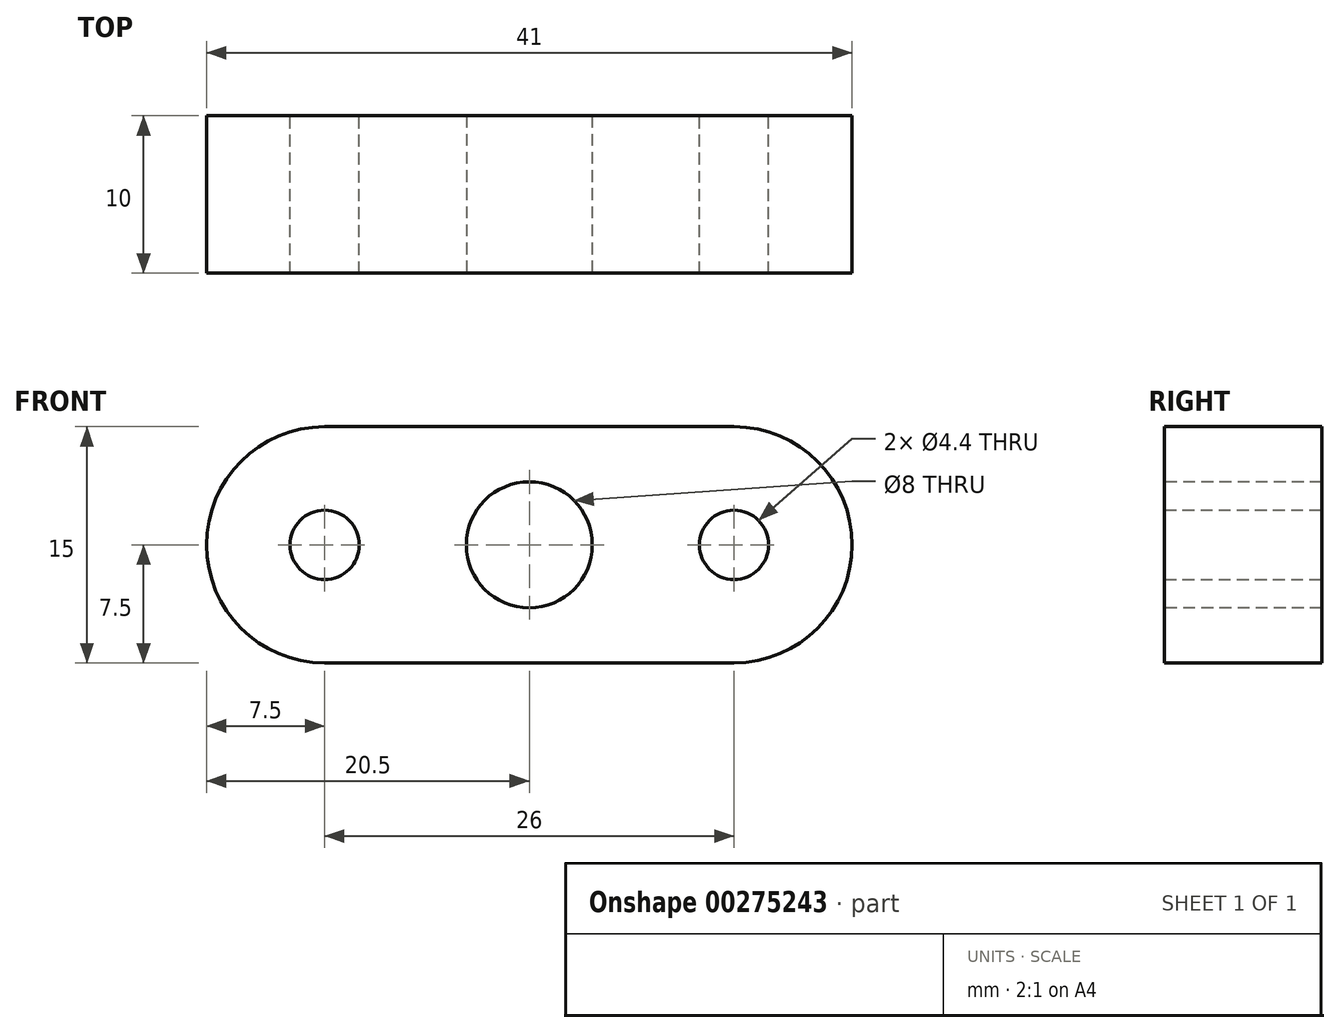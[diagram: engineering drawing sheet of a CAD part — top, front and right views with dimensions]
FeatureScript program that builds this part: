
annotation { "Feature Type Name" : "Feature", "Feature Type Description" : "" }
export const myFeature = defineFeature(function(context is Context, id is Id, definition is map)
    precondition{}
    {
        {
            var Q0;
            Q0=qCreatedBy(makeId("Front.planeOp"),FACE);
            var sketch = newSketch(context, id + "F0", { "sketchPlane" : qUnion([Q0])});
            skCircle(sketch, "E0", {"center": v(0, 0) * mm, "radius": 4 * mm});
            skArc(sketch, "E1", {"start": v(13, -7.5) * mm, "mid": v(20.5, 0) * mm, "end": v(13, 7.5) * mm});
            skArc(sketch, "E2", {"start": v(-13, 7.5) * mm, "mid": v(-20.5, 0) * mm, "end": v(-13, -7.5) * mm});
            skLineSegment(sketch, "E3", {"start": v(-13, 7.5) * mm, "end": v(13, 7.5) * mm});
            skLineSegment(sketch, "E4", {"start": v(-13, -7.5) * mm, "end": v(13, -7.5) * mm});
            skPoint(sketch, "E5", {"position": v(-27, 0) * mm});
            skPoint(sketch, "E6", {"position": v(27, 0) * mm});
            skPoint(sketch, "E6.positionSnap0", {"position": v(22, 0) * mm});
            skSolve(sketch);
        }
        {
            var Q0;
            Q0 = qSketchRegion(id + "F0", true);
            extrude(context, id + "F1", {"entities" : qUnion([Q0]), "oppositeDirection" : true, "depth" : 10 * mm});
        }
        {
            var Q0;
            Q0=sQuery(id+"F0.wireOp",VERTEX,"E2.center");
            var Q1;
            Q1=sQuery(id+"F0.wireOp",VERTEX,"E1.center");
            var Q2;
            Q2=makeQuery(id+"F1.opExtrude","SWEPT_BODY",BODY,{"disambiguationData":[OSD([sQuery(id+"F0.wireOp",EDGE,"E0"),sQuery(id+"F0.wireOp",EDGE,"E1"),sQuery(id+"F0.wireOp",EDGE,"E2"),sQuery(id+"F0.wireOp",EDGE,"E3"),sQuery(id+"F0.wireOp",EDGE,"E4")])]});
            hole(context, id + "F2", {"style" : HoleStyle.SIMPLE, "endStyle" : HoleEndStyle.BLIND, "standardTappedOrClearance" : lookupTablePath({ "standard" : "ISO", "fit" : "Normal", "size" : "M4", "type" : "Clearance" }), "standardBlindInLast" : lookupTablePath({ "fit" : "Standard", "standard" : "ISO", "size" : "M4", "type" : "Clearance" }), "holeDiameter" : 4.4 * mm, "holeDepth" : 10 * mm, "tappedDepth" : 12 * mm, "tapClearance" : 3, "startFromSketch" : true, "locations" : qUnion([Q0, Q1]), "scope" : qUnion([Q2])});
        }
    });
